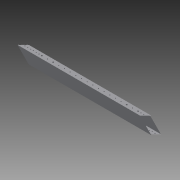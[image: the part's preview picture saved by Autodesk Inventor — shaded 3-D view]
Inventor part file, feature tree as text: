
AUTODESK INVENTOR PART (.ipt)
format: ipt  version: 2015 SP1 (Build 190203100, 203)  size: 220,160 bytes
history: native  units: in
note: dims shown in document units (in); Inventor stores cm internally (conversion verified against a paired STEP export)
features: sketch x4, projected_geometry x3, extrude x2, hole x2, pattern_linear x1
ambient origin geometry x8: Origin, YZ Plane, XZ Plane, XY Plane, X Axis, Y Axis, Z Axis, Center Point
bodies: Solid1 (feature_tree)
feature tree (12):
  extrude  "Extrusion1"  Depth=1.0in
  hole  "Hole1"  [1 undecoded]
  pattern_linear  "Rectangular Pattern1"  Spacing1=28.0in  [1 undecoded]
  extrude  "Extrusion3"  Depth=1.0in
  hole  "Hole2"  [1 undecoded]
  sketch  "Sketch1"  dims[d0=2.0in d1=1.0in]
  sketch  "Sketch2"  dims[d2=1.8in d3=0.8in]
  projected_geometry  "Projected Loop1"
  sketch  "Sketch4"  dims[d4=0.1in]
  projected_geometry  "Projected Loop3"
  sketch  "Sketch5"  dims[d5=0.1in d6=28.0in d7=0.0in d9=0.5in d10=0.5in d11=0.1562in d12=0.75in d13=0.375in d14=0.25in d15=0.5635in d16=1.0in d17=0.8108in d18=11.0236in d20=1.0in d27=0.25in d28=0.25in d29=0.25in d30=0.25in d31=0.25in d32=0.25in d33=1.0in d34=0.0in d35=2.0in d36=3.0in d37=4.0in d38=5.0in d39=0.5in d40=0.5in d41=0.5in d42=0.5in d43=0.5in d44=0.5in d45=0.5in d46=0.5in d47=2.0in d48=3.0in d49=4.0in d50=5.0in d51=0.1562in d52=0.75in d53=0.375in d54=0.25in d55=0.5635in d56=1.0in d57=0.8108in]
  projected_geometry  "Projected Loop4"
note: 3 required parameter values undecoded (feature->parameter linkage not recoverable at this tier; creation-order binding heuristic only, values carry confidence <= 0.55)
